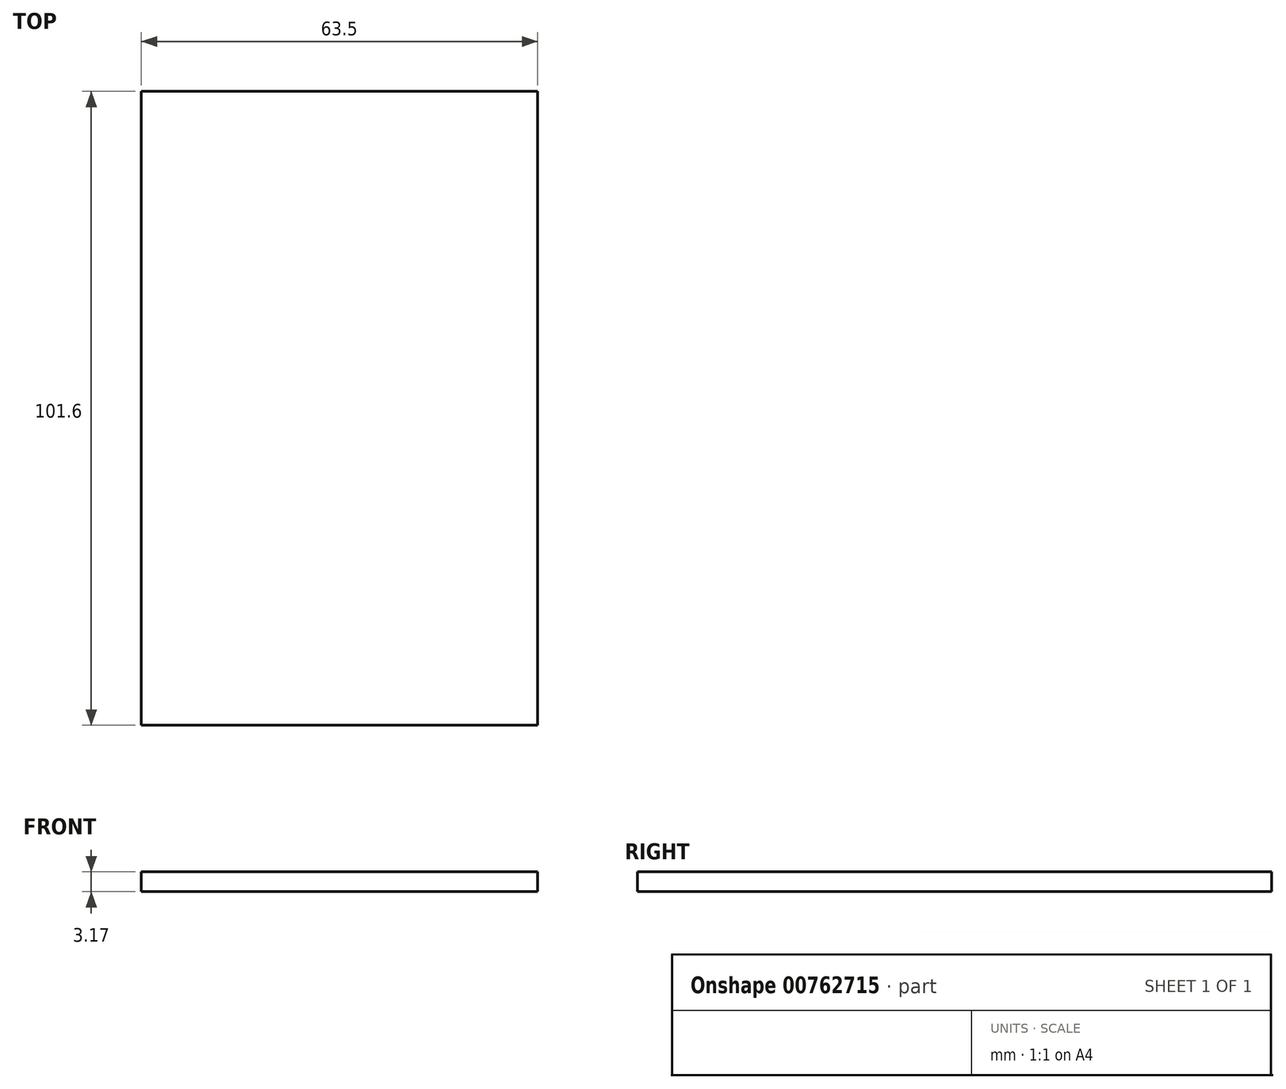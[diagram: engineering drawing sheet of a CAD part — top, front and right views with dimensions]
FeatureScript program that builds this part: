
annotation { "Feature Type Name" : "Feature", "Feature Type Description" : "" }
export const myFeature = defineFeature(function(context is Context, id is Id, definition is map)
    precondition{}
    {
        {
            var Q0;
            Q0=qCreatedBy(makeId("Top.planeOp"),FACE);
            var sketch = newSketch(context, id + "F0", { "sketchPlane" : qUnion([Q0])});
            skLineSegment(sketch, "E0", {"start": v(0, 38.67) * mm, "end": v(31.75, 38.67) * mm});
            skLineSegment(sketch, "E1", {"start": v(0, 38.67) * mm, "end": v(-31.75, 38.67) * mm});
            skLineSegment(sketch, "E2", {"start": v(-31.75, 38.67) * mm, "end": v(-31.75, -62.93) * mm});
            skLineSegment(sketch, "E3", {"start": v(-31.75, -62.93) * mm, "end": v(31.75, -62.93) * mm});
            skLineSegment(sketch, "E4", {"start": v(31.75, -62.93) * mm, "end": v(31.75, 38.67) * mm});
            skSolve(sketch);
        }
        {
            var Q0;
            Q0=makeQuery(id+"F0.imprint","IMPRINT",FACE,{"disambiguationData":[TD([[makeQuery(id+"F0.imprint","IMPRINT",EDGE,{"derivedFrom":sQuery(id+"F0.wireOp",EDGE,"E0")}),-1.0]])]});
            extrude(context, id + "F1", {"entities" : qUnion([Q0]), "depth" : 3.17 * mm, "offsetDistance" : 25.4 * mm});
        }
    });
